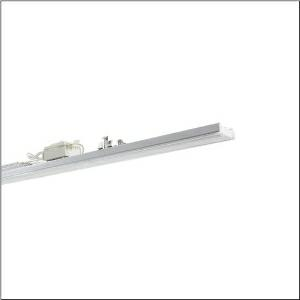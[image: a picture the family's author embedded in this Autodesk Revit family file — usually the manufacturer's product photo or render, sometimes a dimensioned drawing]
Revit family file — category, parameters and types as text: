
# Revit family: licross_11_recessed_ho_51tl1wdv4m2m
name_source: partatom
category: Lighting Fixtures
units: mm (PartAtom-declared; Revit-internal decimal feet)

## family parameters
Cut with Voids When Loaded = No
Host = Face
Light Source = No
Part Type = Normal
Room Calculation Point = No
Round Connector Dimension = Use Diameter
Shared = No

## types (1)
- --- (1 x LED, 27420 lm, 150.5 W, 4000K)
    Apparent Load = 150 VA
    CIE Flux Codes = 73 94 99 100 100
    Color Rendering = 80
    Color Temperature = 4000K
    Default Elevation = 1800 mm
    Description = Licross 11 Recessed HO, luminaire insert, of sheet steel, coil coated, white, length: 2.250mm, width: 66mm, height: 67mm, LED rated luminous flux: 27.420lm, light colour: 840, SDCM (Standard Deviation of Colour Matching)MacAdam ≤ 2 SDCM (initial), control gear: DALI 2, with plug, 5-pole, with phase selection, mains connection: 220..240V, AC, 50/60Hz, rated input power: 151W, internal wiring halogen-free, primary optical cover: cover, of PMMA, light emission: direct distribution, primary light characteristic: symmetric, protection rating (complete): IP40, insulation class (complete): insulation class I (protective earthing), certification: CE, ENEC, VDE, UKCA, protection symbol: D if used in an environment without relevant dust loads with corresponding accessories, impact resistance: IK06, permissible ambient temperature for indoor applications: -40..+35°C, corresponds to IFS (International Featured Standards) requirements for safety and quality in the food industry, reducing of maximum allowable ambient temperature of 5°C with ceiling mounting, LABS conformity tested according to VDMA 24364:2018-05, The light source and the operating device comply with the requirements of the Ecodesign Regulation (EU) 2019/2020 and are replaceable in accordance with this regulation, packaging unit: 1 piece
    Height = 58 mm
    Lamp = 1 x LED
    Lamp Light Flux = 27420 lm
    Lamp Power = 150.5 W
    Lamp count = 1
    Length = 2250 mm
    Luminous efficacy = 182 lm/W
    Manufacturer = Siteco
    ModVariant = No
    Model = 51TL1WDV4M2M
    Mounting Place = Ceiling
    Mounting Type = Pendant
    Number of Poles = 1
    OnlyDefault = Yes
    Power Factor = 1
    Product Name = Licross 11 Recessed HO
    Product group = luminaire insert | ceiling pendant
    ProductGroupID = 901
    Protection Class = Protection class I
    Protection Degree = IP 40
    RLX_Detail_Level = 1
    RLX_Emergency_Light_Flux = 0 lm
    RLX_Emergency_Type = 0
    RLX_Emergency_Type_DB = No
    RlxData = <blob elided: 30093 chars, md5=e991b66b>
    Socket = socket
    Standby Power = 0 W
    System Light Flux = 27420 lm
    System Power = 150 W
    Type Comments = factory setting: luminous flux: 100 % | dim-lin: 254 | 690 mA
    Type Image = l_1296930.jpg
    URL = http://relux.com
    VarID = @adj_065729
    Voltage = 0 V
    Weight = 0.00 kg
    Width = 66 mm

## geometry (parser evidence)
native form markers: Blend x4, Sweep x10
no freeform markers — native parametric forms only
